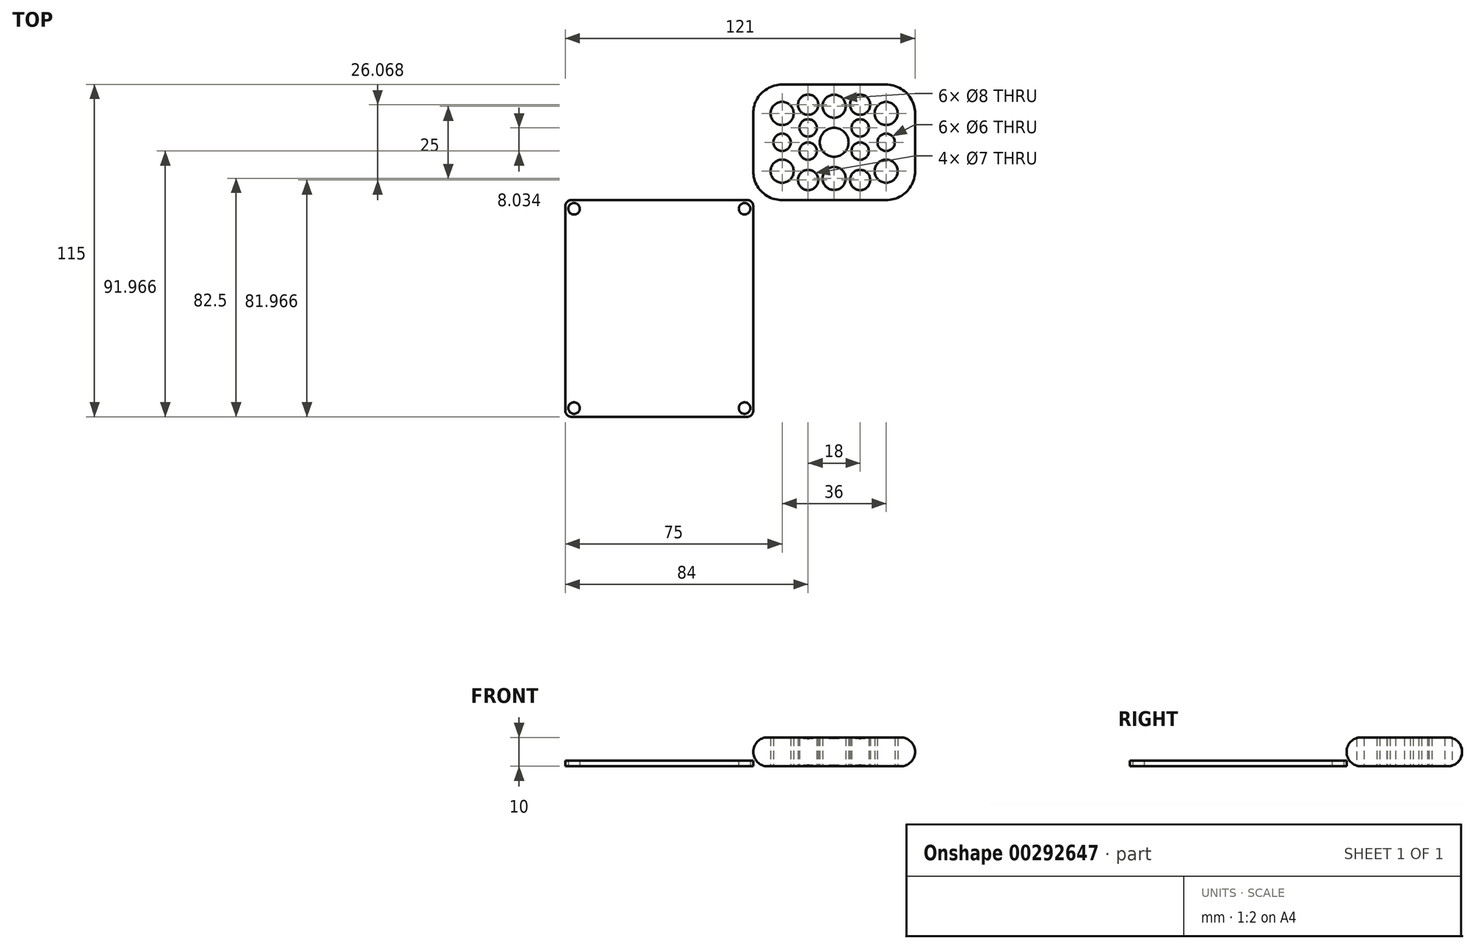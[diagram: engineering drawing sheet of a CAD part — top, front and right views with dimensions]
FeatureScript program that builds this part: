
annotation { "Feature Type Name" : "Feature", "Feature Type Description" : "" }
export const myFeature = defineFeature(function(context is Context, id is Id, definition is map)
    precondition{}
    {
        {
            var Q0;
            Q0=qCreatedBy(makeId("Top.planeOp"),FACE);
            var sketch = newSketch(context, id + "F0", { "sketchPlane" : qUnion([Q0])});
            skLineSegment(sketch, "E0.bottom", {"start": v(10, 0) * mm, "end": v(46, 0) * mm});
            skLineSegment(sketch, "E0.top", {"start": v(10, 40) * mm, "end": v(46, 40) * mm});
            skLineSegment(sketch, "E0.left", {"start": v(0, 10) * mm, "end": v(0, 30) * mm});
            skLineSegment(sketch, "E0.right", {"start": v(56, 10) * mm, "end": v(56, 30) * mm});
            skPoint(sketch, "E1.visualSharp", {"position": v(0, 40) * mm});
            skArc(sketch, "E1.filletArc", {"start": v(10, 40) * mm, "mid": v(2.93, 37.07) * mm, "end": v(0, 30) * mm});
            skPoint(sketch, "E2.visualSharp", {"position": v(0, 0) * mm});
            skArc(sketch, "E2.filletArc", {"start": v(0, 10) * mm, "mid": v(2.93, 2.93) * mm, "end": v(10, 0) * mm});
            skPoint(sketch, "E3.visualSharp", {"position": v(56, 0) * mm});
            skArc(sketch, "E3.filletArc", {"start": v(46, 0) * mm, "mid": v(53.07, 2.93) * mm, "end": v(56, 10) * mm});
            skPoint(sketch, "E4.visualSharp", {"position": v(56, 40) * mm});
            skArc(sketch, "E4.filletArc", {"start": v(56, 30) * mm, "mid": v(53.07, 37.07) * mm, "end": v(46, 40) * mm});
            skCircle(sketch, "E5", {"center": v(10, 30) * mm, "radius": 4 * mm});
            skCircle(sketch, "E6", {"center": v(46, 30) * mm, "radius": 4 * mm});
            skCircle(sketch, "E7", {"center": v(46, 10) * mm, "radius": 4 * mm});
            skCircle(sketch, "E8", {"center": v(10, 10) * mm, "radius": 4 * mm});
            skLineSegment(sketch, "E9", {"start": v(28, 5) * mm, "end": v(28, 10) * mm});
            skCircle(sketch, "E10", {"center": v(28, 7.5) * mm, "radius": 4 * mm});
            skCircle(sketch, "E11.MirrorC", {"center": v(28, 32.5) * mm, "radius": 4 * mm});
            skCircle(sketch, "E12", {"center": v(46, 20) * mm, "radius": 3 * mm});
            skCircle(sketch, "E13", {"center": v(10, 20) * mm, "radius": 3 * mm});
            skCircle(sketch, "E14", {"center": v(37, 25) * mm, "radius": 3 * mm});
            skCircle(sketch, "E15.MirrorC", {"center": v(19, 25) * mm, "radius": 3 * mm});
            skCircle(sketch, "E16.MirrorC", {"center": v(19, 16.97) * mm, "radius": 3 * mm});
            skCircle(sketch, "E17", {"center": v(28, 20) * mm, "radius": 5 * mm});
            skLineSegment(sketch, "E18", {"start": v(19, 16.97) * mm, "end": v(19, 6.97) * mm});
            skCircle(sketch, "E19", {"center": v(19, 6.97) * mm, "radius": 3.5 * mm});
            skLineSegment(sketch, "E20", {"start": v(28, 20) * mm, "end": v(24.67, 20) * mm});
            skCircle(sketch, "E21.MirrorC", {"center": v(19, 33.03) * mm, "radius": 3.5 * mm});
            skCircle(sketch, "E22.MirrorC", {"center": v(37, 6.97) * mm, "radius": 3.5 * mm});
            skCircle(sketch, "E23.MirrorC", {"center": v(37, 33.03) * mm, "radius": 3.5 * mm});
            skCircle(sketch, "E24.MirrorC", {"center": v(37, 16.97) * mm, "radius": 3 * mm});
            skSolve(sketch);
        }
        {
            var Q0;
            Q0=makeQuery(id+"F0.imprint","IMPRINT",FACE,{"disambiguationData":[TD([[makeQuery(id+"F0.imprint","IMPRINT",EDGE,{"derivedFrom":sQuery(id+"F0.wireOp",EDGE,"E0.bottom")}),1.0]])]});
            extrude(context, id + "F1", {"entities" : qUnion([Q0]), "offsetDistance" : 25 * mm, "depth" : 10 * mm});
        }
        {
            var Q0;
            Q0=qCreatedBy(makeId("Top.planeOp"),FACE);
            var sketch = newSketch(context, id + "F2", { "sketchPlane" : qUnion([Q0])});
            skLineSegment(sketch, "E25.bottom", {"start": v(-2, 0) * mm, "end": v(-63, 0) * mm});
            skLineSegment(sketch, "E25.top", {"start": v(-2, -75) * mm, "end": v(-63, -75) * mm});
            skLineSegment(sketch, "E25.left", {"start": v(0, -2) * mm, "end": v(0, -73) * mm});
            skLineSegment(sketch, "E25.right", {"start": v(-65, -2) * mm, "end": v(-65, -73) * mm});
            skLineSegment(sketch, "E26", {"start": v(-32.5, 0) * mm, "end": v(-32.5, -75) * mm});
            skLineSegment(sketch, "E27", {"start": v(-65, -37.5) * mm, "end": v(0, -37.5) * mm});
            skCircle(sketch, "E28", {"center": v(-62, -3) * mm, "radius": 2 * mm});
            skPoint(sketch, "E29.visualSharp", {"position": v(-65, 0) * mm});
            skArc(sketch, "E29.filletArc", {"start": v(-63, 0) * mm, "mid": v(-64.41, -0.59) * mm, "end": v(-65, -2) * mm});
            skPoint(sketch, "E30.visualSharp", {"position": v(0, 0) * mm});
            skArc(sketch, "E30.filletArc", {"start": v(0, -2) * mm, "mid": v(-0.59, -0.59) * mm, "end": v(-2, 0) * mm});
            skPoint(sketch, "E31.visualSharp", {"position": v(0, -75) * mm});
            skArc(sketch, "E31.filletArc", {"start": v(-2, -75) * mm, "mid": v(-0.59, -74.41) * mm, "end": v(0, -73) * mm});
            skPoint(sketch, "E32.visualSharp", {"position": v(-65, -75) * mm});
            skArc(sketch, "E32.filletArc", {"start": v(-65, -73) * mm, "mid": v(-64.41, -74.41) * mm, "end": v(-63, -75) * mm});
            skCircle(sketch, "E33.MirrorC", {"center": v(-3, -3) * mm, "radius": 2 * mm});
            skCircle(sketch, "E34.MirrorC", {"center": v(-62, -72) * mm, "radius": 2 * mm});
            skCircle(sketch, "E35.MirrorC", {"center": v(-3, -72) * mm, "radius": 2 * mm});
            skSolve(sketch);
        }
        {
            var Q0;
            Q0=makeQuery(id+"F2.imprint","IMPRINT",FACE,{"disambiguationData":[TD([[makeQuery(id+"F2.imprint","IMPRINT",EDGE,{"derivedFrom":sQuery(id+"F2.wireOp",EDGE,"E28")}),-1.0]])]});
            var Q1;
            {var subQ5=sQuery(id+"F2.wireOp",EDGE,"E30.filletArc");Q1=makeQuery(id+"F2.imprint","IMPRINT",FACE,{"disambiguationData":[TD([[makeQuery(id+"F2.imprint","IMPRINT",EDGE,{"derivedFrom":subQ5}),1.0]])]});}
            var Q2;
            {var subQ7=sQuery(id+"F2.wireOp",EDGE,"E32.filletArc");Q2=makeQuery(id+"F2.imprint","IMPRINT",FACE,{"disambiguationData":[TD([[makeQuery(id+"F2.imprint","IMPRINT",EDGE,{"derivedFrom":subQ7}),1.0]])]});}
            var Q3;
            {var subQ7=sQuery(id+"F2.wireOp",EDGE,"E31.filletArc");Q3=makeQuery(id+"F2.imprint","IMPRINT",FACE,{"disambiguationData":[TD([[makeQuery(id+"F2.imprint","IMPRINT",EDGE,{"derivedFrom":subQ7}),1.0]])]});}
            extrude(context, id + "F3", {"entities" : qUnion([Q0, Q1, Q2, Q3]), "depth" : 2 * mm});
        }
        {
            var Q0;
            Q0=makeQuery(id+"F1.opExtrude","CAP_EDGE",EDGE,{"disambiguationData":[OSD([sQuery(id+"F0.wireOp",EDGE,"E0.bottom")])],"isStart":false});
            var Q1;
            Q1=makeQuery(id+"F1.opExtrude","CAP_EDGE",EDGE,{"disambiguationData":[OSD([sQuery(id+"F0.wireOp",EDGE,"E3.filletArc")])],"isStart":false});
            var Q2;
            Q2=makeQuery(id+"F1.opExtrude","CAP_EDGE",EDGE,{"disambiguationData":[OSD([sQuery(id+"F0.wireOp",EDGE,"E0.bottom")])],"isStart":true});
            fillet(context, id + "F4", {"entities" : qUnion([Q0, Q1, Q2]), "tangentPropagation" : true, "radius" : 5 * mm, "defaultsChanged" : false, "vertexSettings" : [], "allowEdgeOverflow" : false});
        }
    });
